# Revit family: 1
name_source: partatom
category: Pipe Accessories
revit_build: Autodesk Revit 2018 (Build: 20190510_1515(x64)
units: mm (PartAtom-declared; Revit-internal decimal feet)

## family parameters
Always vertical = No
Cut with Voids When Loaded = No
OmniClass Number = 23.65.00.00
OmniClass Title = Supply and Distribution of Liquids and Gases
Part Type = Normal
Round Connector Dimension = Use Diameter
Shared = No
Work Plane-Based = No

## types (1)
- 3/4" - Male thermostatic mixing valve for solar applications
    Antifreeze: = Passiveted Propylene Glycol
    Application fluids = Water or glycol solutions
    BIMobject category = Plumbing Valves
    Brand url = www.pintossi.it
    Conditioning: = as indicated by the producer
    Copper (CU): = < 0,1 mg/kg (< 0,05 mg/kg for steam)
    Description = Pintossi+C Solar thermostatic mixing valve is designed for use in domestic water as well as heating systems.

The main function is to maintain constant, to a set value, the mixed water temperature, regardless of any variation of temperature and pressure of hot and cold water supply.

An anti-burn function is provided by the valve, stopping the hot mixed water delivery in case of unexpeted interruption of the inlet cold water supply, avoiding potentials burns. Thanks to this and anti-burining function the valve is particular indicated in public buildings like schools and hospitals for the presence of individuals at risk.

Thanks to high water temperatures allowed, the valve is suitable to be used in solar systems or in standard systems where the hot inlet water can reach high termperatures.
    Design country = Italy
    Edition number = 0
    Fluid aspect: = Limpid
    IFC Classification = Valve
    Iron (FE): = < 0,5 mg/kg (< 0,1 mg/kg for steam)
    Main Inlet/Outlet Diameter = 19 mm
    Manufacturer = Pintossi+C
    Manufacturer country = Italy
    Manufacturer name = Pintossi+C
    Masterformat 2014 Code = 23 00 00
    Masterformat 2014 Description = Heating, Ventilating, and Air Conditioning (HVAC)
    Material Blue = Pintossi - Plastic - Blue ABS
    Material Body = Pintossi - Metal - Brass
    Material Cap = Pintossi - Plastic - Yellow ABS
    Material Red = Pintossi - Plastic - Red ABS
    Material main = Brass
    Max hot inlet water temp = 100 °C
    Maximum percentage of glycol [%] = 30
    Maximum working pressure = 10.0 bar
    Maximum working temperature = 100 °C
    Min cold inlet water temp = 4 °C
    Mixed water range = 27 °C - 55 °C
    Model = 3/4" - Male thermostatic mixing valve for solar applications
    NBS Reference Code = 94-94-xx
    NBS Reference Description = Thermostatic Mixinh Valves
    OmniClass Code = 23-27 31 29
    OmniClass Description = Mixing Valves
    PH: = Between 7 and 8Between 7 and 8
    Product Guid = 9c0c1833-9f53-46b7-a094-18835833f6c7
    Product SKU = 1561-SOLAR-THERMOSTATIC-MIXING-VALVE
    Product data url = https://www.bimobject.com
    Product family = COMPONENTS FOR CENTRAL HEATING SYSTEMS
    Product group = THERMOSTATIC MIXING VALVES
    UNSPSC Code = 401416
    URL = www.pintossi.it
    Uniclass 1.4 Code = L71177
    Uniclass 1.4 Description = Mixing valves
    Uniclass 2.0 Code = PR-94-94-xx
    Uniclass 2.0 Description = Thermostatic Mixing Valves
    Uniclass 2015 Code = Pr_65_57_96
    Uniclass 2015 Name = Water filters and strainres
    Uniformat II Code = D30
    Uniformat II Description = HVAC
    Weight Net (Kg) = 0

## geometry (parser evidence)
native form markers: Sweep x3
no freeform markers — native parametric forms only
